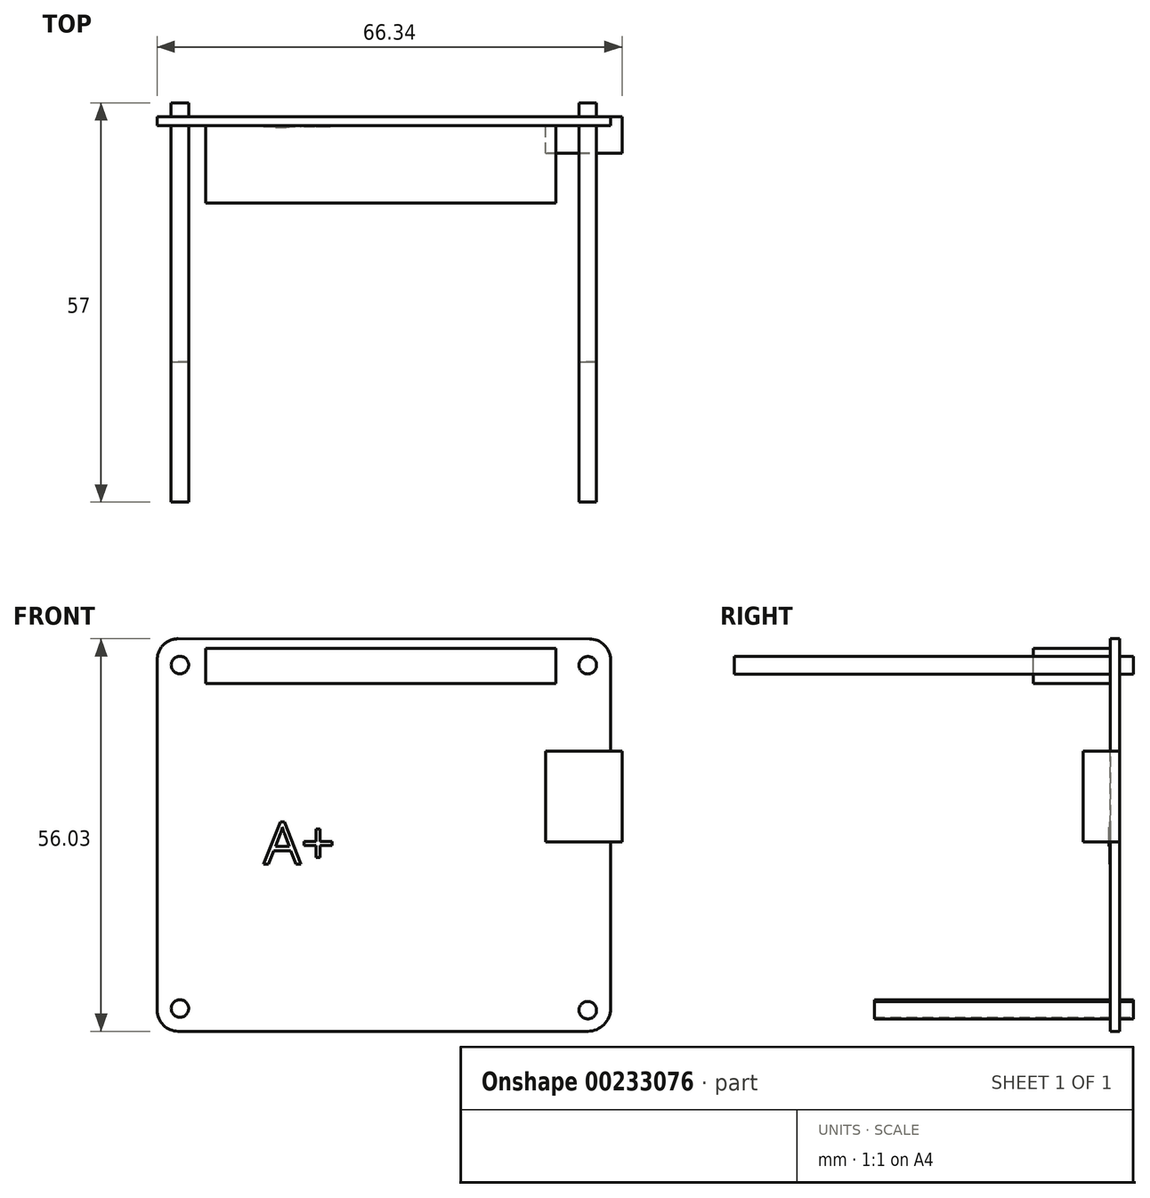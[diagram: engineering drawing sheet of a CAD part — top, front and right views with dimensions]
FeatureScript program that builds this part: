
annotation { "Feature Type Name" : "Feature", "Feature Type Description" : "" }
export const myFeature = defineFeature(function(context is Context, id is Id, definition is map)
    precondition{}
    {
        {
            var Q0;
            Q0=qCreatedBy(makeId("Front.planeOp"),FACE);
            var sketch = newSketch(context, id + "F0", { "sketchPlane" : qUnion([Q0])});
            skLineSegment(sketch, "E0", {"start": v(31.55, 21.56) * mm, "end": v(31.55, -28.2) * mm});
            skLineSegment(sketch, "E1", {"start": v(28.3, -31.44) * mm, "end": v(-30.15, -31.44) * mm});
            skLineSegment(sketch, "E2", {"start": v(28.55, 24.56) * mm, "end": v(-30.15, 24.59) * mm});
            skLineSegment(sketch, "E3", {"start": v(31.55, 24.56) * mm, "end": v(31.55, 20.8) * mm, "construction": true});
            skPoint(sketch, "E4.visualSharp", {"position": v(-33.15, 24.59) * mm});
            skArc(sketch, "E4.filletArc", {"start": v(-30.15, 24.59) * mm, "mid": v(-32.28, 23.7) * mm, "end": v(-33.15, 21.59) * mm});
            skPoint(sketch, "E5.visualSharp", {"position": v(-33.15, -31.44) * mm});
            skArc(sketch, "E5.filletArc", {"start": v(-33.15, -28.44) * mm, "mid": v(-32.28, -30.56) * mm, "end": v(-30.15, -31.44) * mm});
            skPoint(sketch, "E6.visualSharp", {"position": v(31.55, -31.44) * mm});
            skArc(sketch, "E6.filletArc", {"start": v(28.3, -31.44) * mm, "mid": v(30.6, -30.5) * mm, "end": v(31.55, -28.2) * mm});
            skPoint(sketch, "E7.visualSharp", {"position": v(31.55, 24.56) * mm});
            skArc(sketch, "E7.filletArc", {"start": v(31.55, 21.56) * mm, "mid": v(30.67, 23.68) * mm, "end": v(28.55, 24.56) * mm});
            skLineSegment(sketch, "E8", {"start": v(31.55, 20.8) * mm, "end": v(28.3, 20.8) * mm});
            skCircle(sketch, "E9", {"center": v(28.3, 20.8) * mm, "radius": 1.25 * mm});
            skLineSegment(sketch, "E10", {"start": v(31.55, -31.44) * mm, "end": v(31.55, -28.2) * mm, "construction": true});
            skLineSegment(sketch, "E11", {"start": v(28.3, 20.8) * mm, "end": v(28.3, -45.28) * mm, "construction": true});
            skLineSegment(sketch, "E12", {"start": v(31.55, -28.2) * mm, "end": v(28.3, -28.2) * mm, "construction": true});
            skLineSegment(sketch, "E13", {"start": v(-33.15, -31.44) * mm, "end": v(-29.9, -31.44) * mm, "construction": true});
            skLineSegment(sketch, "E14", {"start": v(-22.27, 24.58) * mm, "end": v(-22.27, 18.18) * mm, "construction": true});
            skLineSegment(sketch, "E15", {"start": v(-33.15, 18.18) * mm, "end": v(-26.25, 18.18) * mm, "construction": true});
            skLineSegment(sketch, "E16", {"start": v(-26.25, 18.18) * mm, "end": v(-26.25, 23.18) * mm});
            skLineSegment(sketch, "E17", {"start": v(-26.25, 18.18) * mm, "end": v(23.75, 18.18) * mm});
            skLineSegment(sketch, "E18", {"start": v(23.75, 18.18) * mm, "end": v(23.75, 23.18) * mm});
            skLineSegment(sketch, "E19", {"start": v(-26.25, 23.18) * mm, "end": v(23.75, 23.18) * mm});
            skCircle(sketch, "E20", {"center": v(28.3, -28.43) * mm, "radius": 1.25 * mm});
            skCircle(sketch, "E21", {"center": v(-29.9, -28.2) * mm, "radius": 1.25 * mm});
            skLineSegment(sketch, "E22", {"start": v(-30.15, 24.59) * mm, "end": v(-30.15, 20.84) * mm, "construction": true});
            skLineSegment(sketch, "E23", {"start": v(-29.9, -31.44) * mm, "end": v(-29.9, 27.6) * mm, "construction": true});
            skLineSegment(sketch, "E24", {"start": v(-30.15, 20.84) * mm, "end": v(-29.27, 20.84) * mm, "construction": true});
            skCircle(sketch, "E25", {"center": v(-29.9, 20.84) * mm, "radius": 1.25 * mm});
            skLineSegment(sketch, "E26", {"start": v(-33.15, 21.59) * mm, "end": v(-33.15, -28.44) * mm});
            skLineSegment(sketch, "E27", {"start": v(31.55, 24.56) * mm, "end": v(31.55, 8.56) * mm, "construction": true});
            skLineSegment(sketch, "E28", {"start": v(31.55, 8.56) * mm, "end": v(22.3, 8.56) * mm, "construction": true});
            skLineSegment(sketch, "E29", {"start": v(22.3, 8.56) * mm, "end": v(33.19, 8.56) * mm});
            skLineSegment(sketch, "E30", {"start": v(33.19, 8.56) * mm, "end": v(33.19, -4.44) * mm});
            skLineSegment(sketch, "E31", {"start": v(33.19, -4.44) * mm, "end": v(22.3, -4.44) * mm});
            skLineSegment(sketch, "E32", {"start": v(22.3, -4.44) * mm, "end": v(22.3, 8.56) * mm});
            skText(sketch, "E33", { "text": "A+", "fontName": "OpenSans-Regular.ttf"});
            skLineSegment(sketch, "E34", {"start": v(31.55, 24.56) * mm, "end": v(31.55, -3.32) * mm, "construction": true});
            const initialGuessF0  = {"E33": [-0.01796, -0.0076, 1, 0, 0.00608]};
            skSetInitialGuess(sketch, initialGuessF0);
            skSolve(sketch);
        }
        {
            var Q0;
            Q0=makeQuery(id+"F0.imprint","IMPRINT",FACE,{"disambiguationData":[TD([[makeQuery(id+"F0.imprint","IMPRINT",EDGE,{"derivedFrom":sQuery(id+"F0.wireOp",EDGE,"E1")}),-1.0]])]});
            extrude(context, id + "F1", {"entities" : qUnion([Q0]), "depth" : 1.3 * mm});
        }
        {
            var Q0;
            Q0=makeQuery(id+"F0.imprint","IMPRINT",FACE,{"disambiguationData":[TD([[makeQuery(id+"F0.imprint","IMPRINT",EDGE,{"derivedFrom":sQuery(id+"F0.wireOp",EDGE,"E16")}),-1.0]])]});
            extrude(context, id + "F2", {"entities" : qUnion([Q0]), "operationType" : NewBodyOperationType.ADD, "depth" : 12.3 * mm});
        }
        {
            var Q0;
            {var subQ5=sQuery(id+"F0.wireOp",EDGE,"E32");Q0=makeQuery(id+"F0.imprint","IMPRINT",FACE,{"disambiguationData":[TD([[makeQuery(id+"F0.imprint","IMPRINT",EDGE,{"derivedFrom":subQ5}),-1.0]])]});}
            var Q1;
            {var subQ5=sQuery(id+"F0.wireOp",EDGE,"E30");Q1=makeQuery(id+"F0.imprint","IMPRINT",FACE,{"disambiguationData":[TD([[makeQuery(id+"F0.imprint","IMPRINT",EDGE,{"derivedFrom":subQ5}),-1.0]])]});}
            extrude(context, id + "F3", {"entities" : qUnion([Q0, Q1]), "operationType" : NewBodyOperationType.ADD, "depth" : 5.2 * mm});
        }
        {
            var Q0;
            Q0=makeQuery(id+"F0.imprint","IMPRINT",FACE,{"disambiguationData":[TD([[makeQuery(id+"F0.imprint","IMPRINT",EDGE,{"derivedFrom":sQuery(id+"F0.wireOp",EDGE,"E33.sketch_text.stroke-0")}),-1.0]])]});
            var Q1;
            Q1=makeQuery(id+"F0.imprint","IMPRINT",FACE,{"disambiguationData":[TD([[makeQuery(id+"F0.imprint","IMPRINT",EDGE,{"derivedFrom":sQuery(id+"F0.wireOp",EDGE,"E33.sketch_text.stroke-8")}),1.0]])]});
            var Q2;
            Q2=makeQuery(id+"F0.imprint","IMPRINT",FACE,{"disambiguationData":[TD([[makeQuery(id+"F0.imprint","IMPRINT",EDGE,{"derivedFrom":sQuery(id+"F0.wireOp",EDGE,"E33.sketch_text.stroke-13")}),-1.0]])]});
            extrude(context, id + "F4", {"entities" : qUnion([Q0, Q1, Q2]), "operationType" : NewBodyOperationType.ADD, "depth" : 1.4 * mm});
        }
        {
            var Q0;
            Q0=makeQuery(id+"F0.imprint","IMPRINT",FACE,{"disambiguationData":[TD([[makeQuery(id+"F0.imprint","IMPRINT",EDGE,{"derivedFrom":sQuery(id+"F0.wireOp",EDGE,"E33.sketch_text.stroke-8")}),1.0]])]});
            extrude(context, id + "F5", {"entities" : qUnion([Q0]), "operationType" : NewBodyOperationType.ADD, "depth" : 1.5 * mm});
        }
        {
            var Q0;
            Q0=makeQuery(id+"F0.imprint","IMPRINT",FACE,{"disambiguationData":[TD([[makeQuery(id+"F0.imprint","IMPRINT",EDGE,{"derivedFrom":sQuery(id+"F0.wireOp",EDGE,"E9")}),1.0]])]});
            var Q1;
            Q1=makeQuery(id+"F0.imprint","IMPRINT",FACE,{"disambiguationData":[TD([[makeQuery(id+"F0.imprint","IMPRINT",EDGE,{"derivedFrom":sQuery(id+"F0.wireOp",EDGE,"E25")}),1.0]])]});
            extrude(context, id + "F6", {"entities" : qUnion([Q0, Q1]), "operationType" : NewBodyOperationType.ADD, "depth" : 55 * mm, "hasSecondDirection" : true, "secondDirectionOppositeDirection" : true, "secondDirectionDepth" : 2 * mm});
        }
        {
            var Q0;
            Q0=makeQuery(id+"F0.imprint","IMPRINT",FACE,{"disambiguationData":[TD([[makeQuery(id+"F0.imprint","IMPRINT",EDGE,{"derivedFrom":sQuery(id+"F0.wireOp",EDGE,"E21")}),1.0]])]});
            var Q1;
            Q1=makeQuery(id+"F0.imprint","IMPRINT",FACE,{"disambiguationData":[TD([[makeQuery(id+"F0.imprint","IMPRINT",EDGE,{"derivedFrom":sQuery(id+"F0.wireOp",EDGE,"E20")}),1.0]])]});
            extrude(context, id + "F7", {"entities" : qUnion([Q0, Q1]), "operationType" : NewBodyOperationType.ADD, "depth" : 35 * mm, "hasSecondDirection" : true, "secondDirectionOppositeDirection" : true, "secondDirectionDepth" : 2 * mm});
        }
    });
